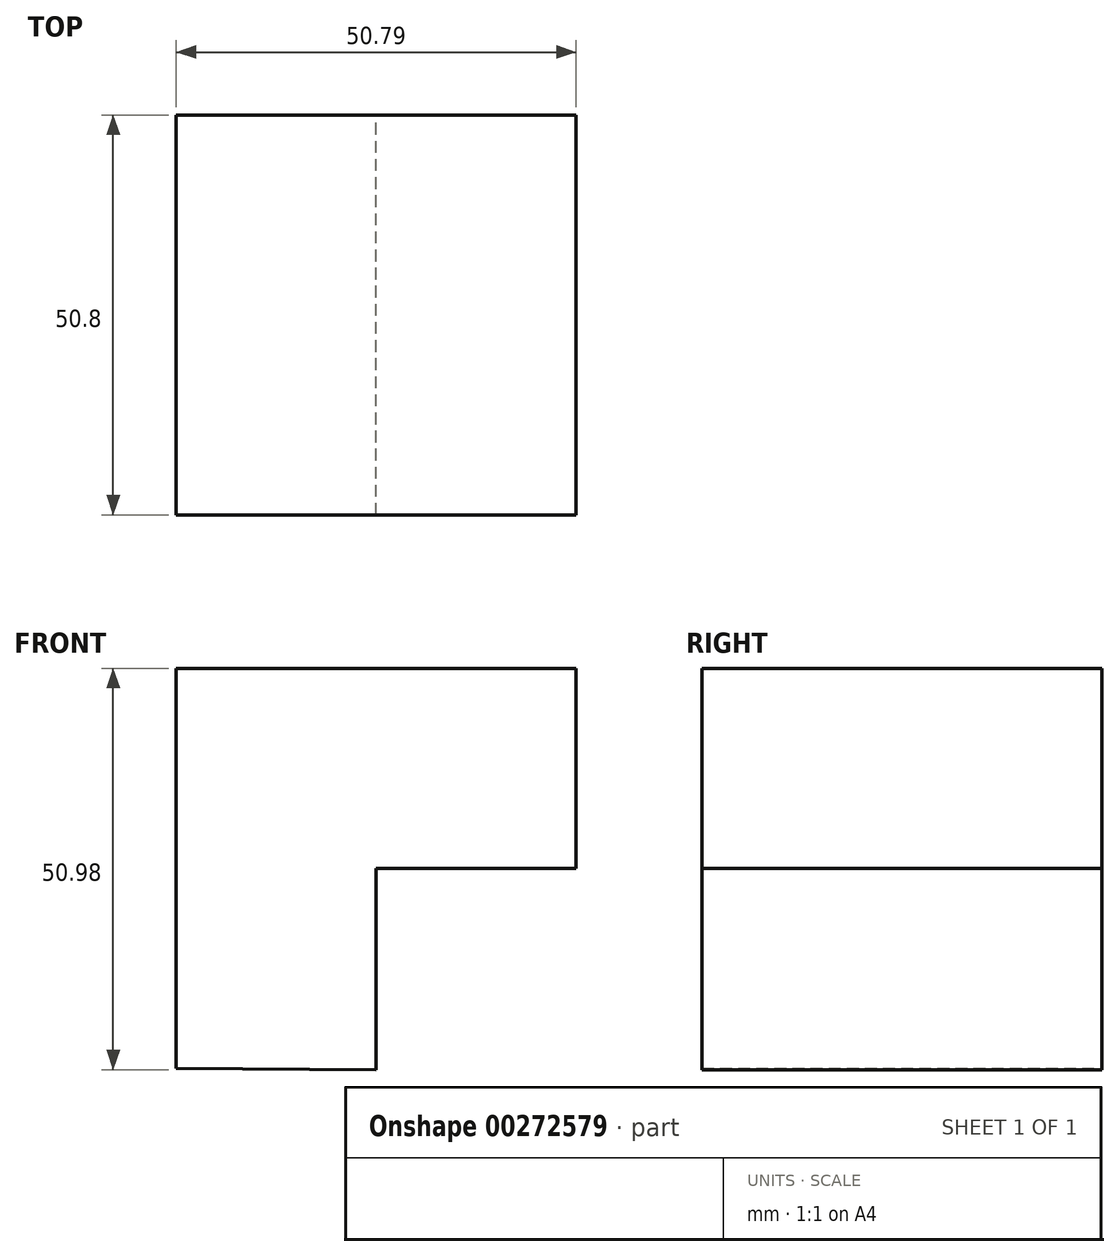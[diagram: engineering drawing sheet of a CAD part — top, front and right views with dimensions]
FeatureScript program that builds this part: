
annotation { "Feature Type Name" : "Feature", "Feature Type Description" : "" }
export const myFeature = defineFeature(function(context is Context, id is Id, definition is map)
    precondition{}
    {
        {
            var Q0;
            Q0=qCreatedBy(makeId("Front.planeOp"),FACE);
            var sketch = newSketch(context, id + "F0", { "sketchPlane" : qUnion([Q0])});
            skLineSegment(sketch, "E0", {"start": v(-56.14, 20.05) * mm, "end": v(-56.14, 70.84) * mm});
            skLineSegment(sketch, "E1", {"start": v(-56.14, 70.84) * mm, "end": v(-5.35, 70.84) * mm});
            skLineSegment(sketch, "E2", {"start": v(-5.35, 70.84) * mm, "end": v(-5.35, 45.45) * mm});
            skLineSegment(sketch, "E3", {"start": v(-5.35, 45.45) * mm, "end": v(-30.74, 45.45) * mm});
            skLineSegment(sketch, "E4", {"start": v(-30.74, 45.45) * mm, "end": v(-30.74, 19.86) * mm});
            skLineSegment(sketch, "E5", {"start": v(-30.74, 19.86) * mm, "end": v(-56.14, 20.05) * mm});
            skSolve(sketch);
        }
        {
            var Q0;
            Q0 = qSketchRegion(id + "F0", true);
            extrude(context, id + "F1", {"entities" : qUnion([Q0]), "depth" : 50.8 * mm});
        }
    });
